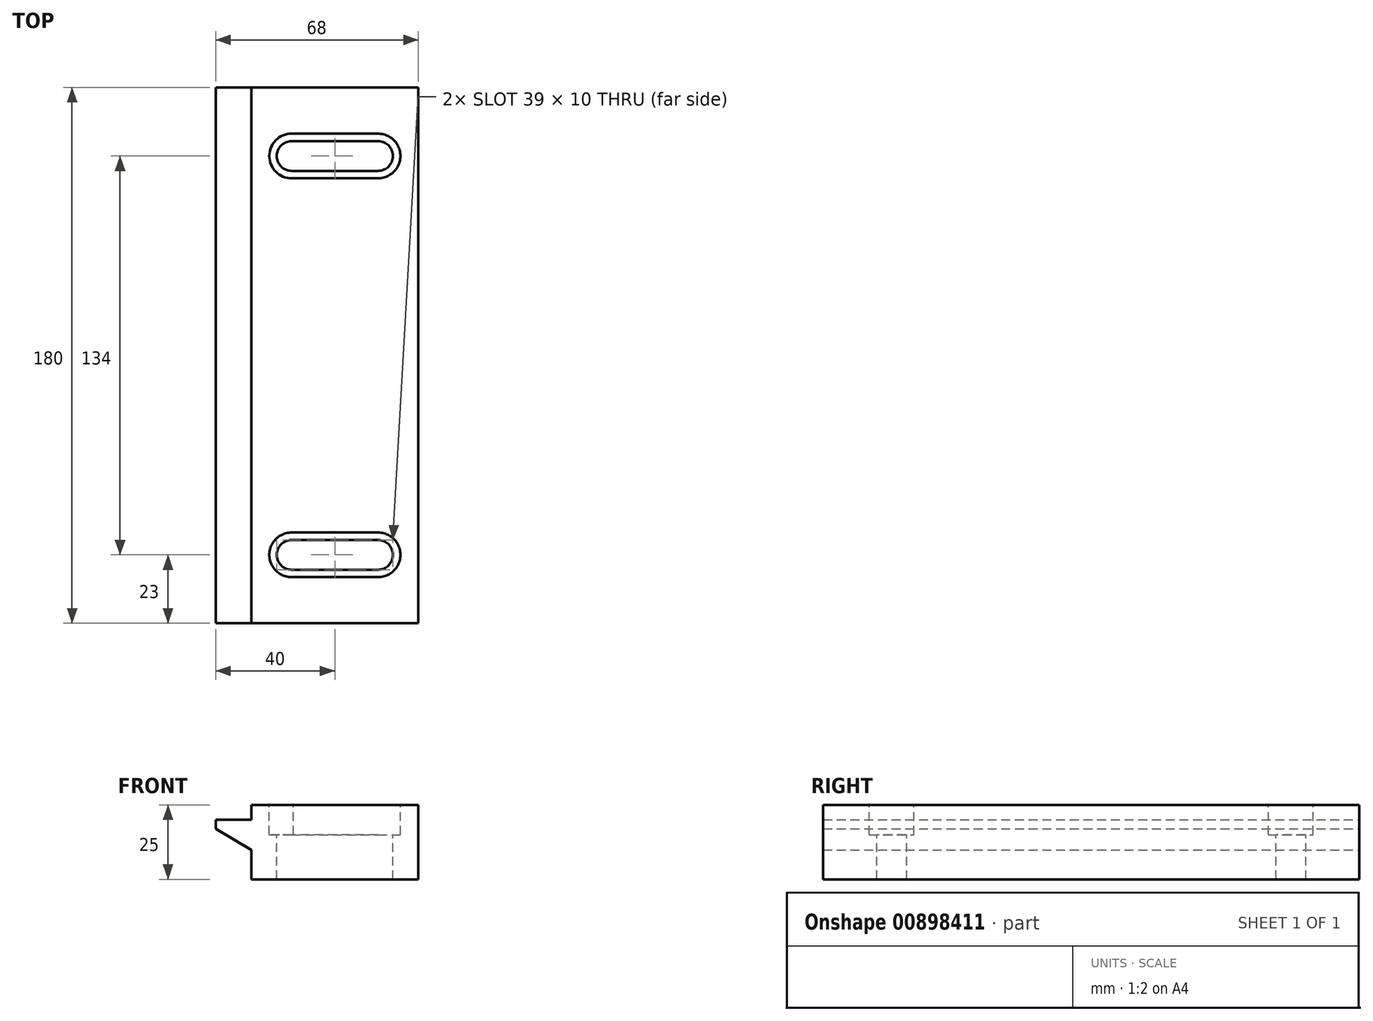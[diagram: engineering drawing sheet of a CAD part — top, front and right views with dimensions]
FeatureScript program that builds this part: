
annotation { "Feature Type Name" : "Feature", "Feature Type Description" : "" }
export const myFeature = defineFeature(function(context is Context, id is Id, definition is map)
    precondition{}
    {
        {
            var Q0;
            Q0=qCreatedBy(makeId("Front.planeOp"),FACE);
            var sketch = newSketch(context, id + "F0", { "sketchPlane" : qUnion([Q0])});
            skLineSegment(sketch, "E0", {"start": v(0, 0) * mm, "end": v(56, 0) * mm});
            skLineSegment(sketch, "E1", {"start": v(56, 0) * mm, "end": v(56, -25) * mm});
            skLineSegment(sketch, "E2", {"start": v(0, 0) * mm, "end": v(0, -5) * mm});
            skLineSegment(sketch, "E3", {"start": v(56, -25) * mm, "end": v(0, -25) * mm});
            skLineSegment(sketch, "E4", {"start": v(0, -25) * mm, "end": v(0, -17) * mm});
            skLineSegment(sketch, "E5", {"start": v(0, -5) * mm, "end": v(-12, -5) * mm});
            skLineSegment(sketch, "E6", {"start": v(-12, -5) * mm, "end": v(-12, -8) * mm});
            skLineSegment(sketch, "E7", {"start": v(-12, -8) * mm, "end": v(0, -15.2) * mm});
            skLineSegment(sketch, "E8", {"start": v(0, -17) * mm, "end": v(0, -15.2) * mm});
            skSolve(sketch);
        }
        {
            var Q0;
            Q0 = qSketchRegion(id + "F0", true);
            extrude(context, id + "F1", {"entities" : qUnion([Q0]), "depth" : 180 * mm, "offsetDistance" : 25 * mm});
        }
        {
            var Q0;
            Q0=makeQuery(id+"F1.opExtrude","SWEPT_FACE",FACE,{"disambiguationData":[OSD([sQuery(id+"F0.wireOp",EDGE,"E0")])]});
            var sketch = newSketch(context, id + "F2", { "sketchPlane" : qUnion([Q0])});
            skArc(sketch, "E9", {"start": v(42.47, -164.5) * mm, "mid": v(50, -157) * mm, "end": v(42.47, -149.5) * mm});
            skLineSegment(sketch, "E10", {"start": v(42.5, -157) * mm, "end": v(42.47, -157) * mm});
            skLineSegment(sketch, "E11", {"start": v(42.47, -164.5) * mm, "end": v(13.5, -164.5) * mm});
            skArc(sketch, "E12", {"start": v(42.47, -30.5) * mm, "mid": v(50, -23) * mm, "end": v(42.47, -15.5) * mm});
            skLineSegment(sketch, "E13", {"start": v(42.5, -23) * mm, "end": v(42.47, -23) * mm});
            skLineSegment(sketch, "E14", {"start": v(42.47, -30.5) * mm, "end": v(13.5, -30.5) * mm});
            skArc(sketch, "E15", {"start": v(13.5, -15.5) * mm, "mid": v(6, -23) * mm, "end": v(13.5, -30.5) * mm});
            skLineSegment(sketch, "E16", {"start": v(42.47, -15.5) * mm, "end": v(13.5, -15.5) * mm});
            skArc(sketch, "E17", {"start": v(14.04, -149.52) * mm, "mid": v(6, -156.73) * mm, "end": v(13.5, -164.5) * mm});
            skLineSegment(sketch, "E18", {"start": v(42.47, -149.5) * mm, "end": v(14.04, -149.52) * mm});
            skSolve(sketch);
        }
        {
            var Q0;
            Q0 = qSketchRegion(id + "F2", true);
            extrude(context, id + "F3", {"entities" : qUnion([Q0]), "operationType" : NewBodyOperationType.REMOVE, "oppositeDirection" : true, "depth" : 10 * mm, "offsetDistance" : 25 * mm});
        }
        {
            var Q0;
            Q0=makeQuery(id+"F1.opExtrude","SWEPT_FACE",FACE,{"disambiguationData":[OSD([sQuery(id+"F0.wireOp",EDGE,"E0")])]});
            var sketch = newSketch(context, id + "F4", { "sketchPlane" : qUnion([Q0])});
            skArc(sketch, "E19", {"start": v(13.5, -18) * mm, "mid": v(8.5, -23) * mm, "end": v(13.5, -28) * mm});
            skArc(sketch, "E20", {"start": v(42.5, -28) * mm, "mid": v(47.5, -23) * mm, "end": v(42.5, -18) * mm});
            skLineSegment(sketch, "E21", {"start": v(13.5, -28) * mm, "end": v(42.5, -28) * mm});
            skLineSegment(sketch, "E22", {"start": v(13.5, -18) * mm, "end": v(42.5, -18) * mm});
            skArc(sketch, "E23", {"start": v(13.5, -152) * mm, "mid": v(8.5, -157) * mm, "end": v(13.5, -162) * mm});
            skArc(sketch, "E24", {"start": v(42.5, -162) * mm, "mid": v(47.5, -157) * mm, "end": v(42.5, -152) * mm});
            skLineSegment(sketch, "E25", {"start": v(13.5, -152) * mm, "end": v(42.5, -152) * mm});
            skLineSegment(sketch, "E26", {"start": v(42.5, -162) * mm, "end": v(13.5, -162) * mm});
            skSolve(sketch);
        }
        {
            var Q0;
            Q0 = qSketchRegion(id + "F4", true);
            extrude(context, id + "F5", {"entities" : qUnion([Q0]), "operationType" : NewBodyOperationType.REMOVE, "oppositeDirection" : true, "depth" : 25 * mm, "offsetDistance" : 25 * mm});
        }
    });
